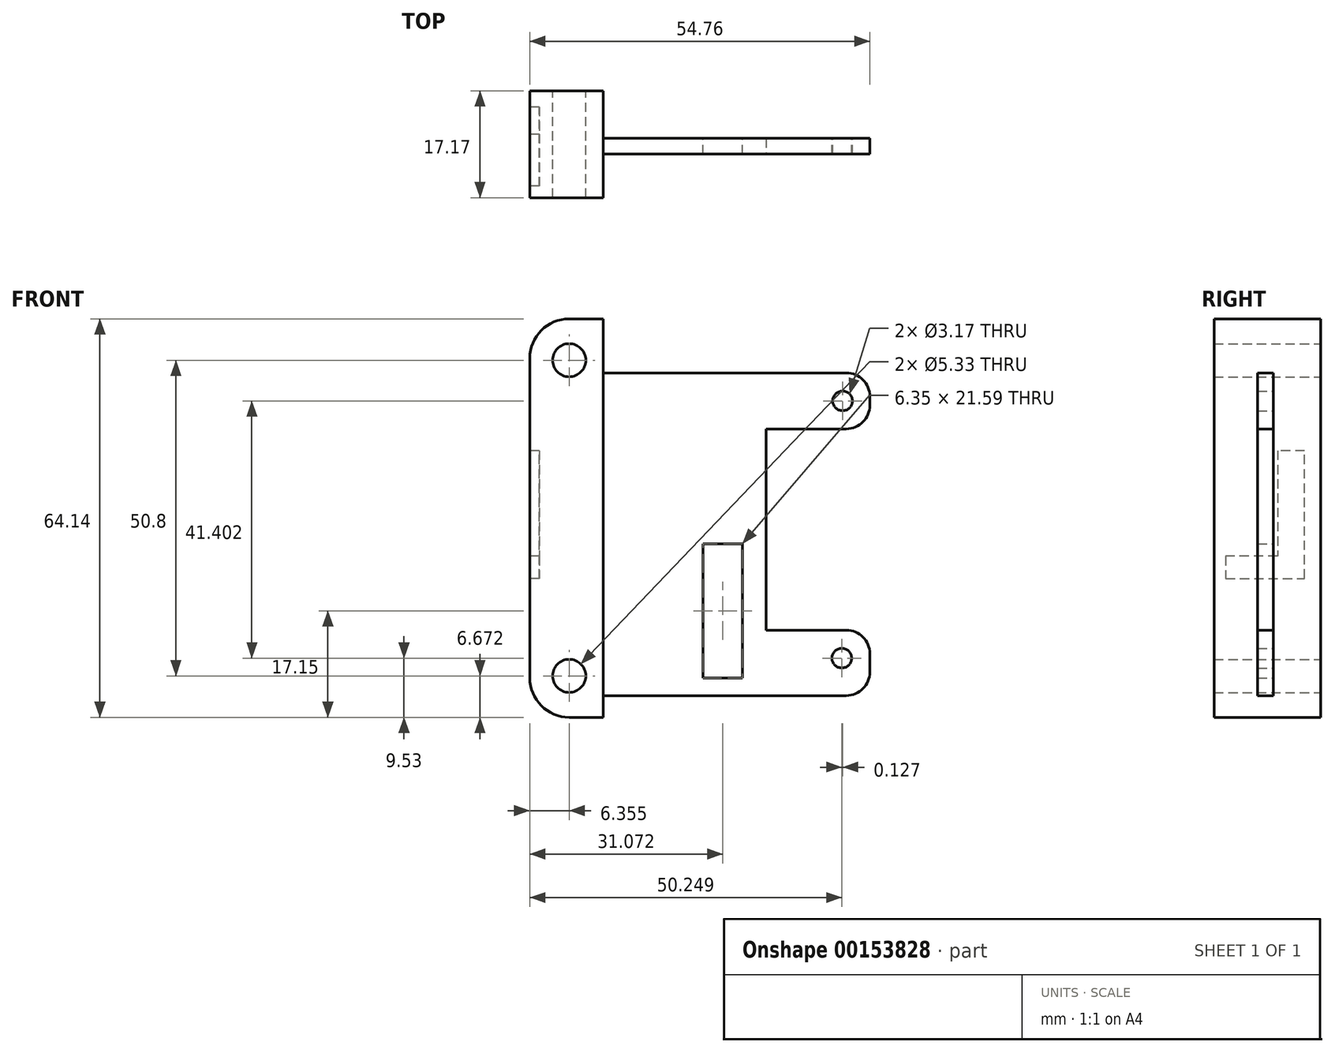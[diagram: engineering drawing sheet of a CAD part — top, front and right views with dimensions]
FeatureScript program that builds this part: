
annotation { "Feature Type Name" : "Feature", "Feature Type Description" : "" }
export const myFeature = defineFeature(function(context is Context, id is Id, definition is map)
    precondition{}
    {
        {
            var Q0;
            Q0=qCreatedBy(makeId("Front.planeOp"),FACE);
            var sketch = newSketch(context, id + "F0", { "sketchPlane" : qUnion([Q0])});
            skCircle(sketch, "E0", {"center": v(-136.53, -6.67) * mm, "radius": 2.67 * mm});
            skCircle(sketch, "E1", {"center": v(-136.53, -57.47) * mm, "radius": 2.67 * mm});
            skLineSegment(sketch, "E2.bottom", {"start": v(-136.53, 0) * mm, "end": v(-85.72, 0) * mm});
            skLineSegment(sketch, "E2.top", {"start": v(-136.53, -64.13) * mm, "end": v(-85.72, -64.13) * mm});
            skLineSegment(sketch, "E2.left", {"start": v(-142.88, -6.35) * mm, "end": v(-142.88, -57.78) * mm});
            skLineSegment(sketch, "E2.right", {"start": v(-85.72, 0) * mm, "end": v(-85.72, -64.13) * mm});
            skPoint(sketch, "E3.visualSharp", {"position": v(-142.88, 0) * mm});
            skArc(sketch, "E3.filletArc", {"start": v(-136.53, 0) * mm, "mid": v(-141.02, -1.86) * mm, "end": v(-142.87, -6.35) * mm});
            skPoint(sketch, "E4.visualSharp", {"position": v(-142.88, -64.13) * mm});
            skArc(sketch, "E4.filletArc", {"start": v(-142.87, -57.78) * mm, "mid": v(-141.02, -62.28) * mm, "end": v(-136.53, -64.13) * mm});
            skCircle(sketch, "E5", {"center": v(-92.5, -13.2) * mm, "radius": 1.59 * mm});
            skLineSegment(sketch, "E6", {"start": v(-136.53, -6.67) * mm, "end": v(-136.53, 0) * mm, "construction": true});
            skLineSegment(sketch, "E7", {"start": v(-136.53, -57.47) * mm, "end": v(-136.53, -64.13) * mm, "construction": true});
            skCircle(sketch, "E8", {"center": v(-92.63, -54.6) * mm, "radius": 1.59 * mm});
            skLineSegment(sketch, "E9.bottom", {"start": v(-114.98, -36.2) * mm, "end": v(-108.63, -36.2) * mm});
            skLineSegment(sketch, "E9.top", {"start": v(-114.98, -57.78) * mm, "end": v(-108.63, -57.78) * mm});
            skLineSegment(sketch, "E9.left", {"start": v(-108.63, -36.2) * mm, "end": v(-108.63, -57.78) * mm});
            skLineSegment(sketch, "E9.right", {"start": v(-114.98, -36.2) * mm, "end": v(-114.98, -57.78) * mm});
            skSolve(sketch);
        }
        {
            var Q0;
            Q0=makeQuery(id+"F0.imprint","IMPRINT",FACE,{"disambiguationData":[TD([[makeQuery(id+"F0.imprint","IMPRINT",EDGE,{"derivedFrom":sQuery(id+"F0.wireOp",EDGE,"E0")}),-1.0]])]});
            var Q1;
            Q1=makeQuery(id+"F0.imprint","IMPRINT",FACE,{"disambiguationData":[TD([[makeQuery(id+"F0.imprint","IMPRINT",EDGE,{"derivedFrom":sQuery(id+"F0.wireOp",EDGE,"01fd989c-5bba-4e2a-9568-51aa30f200c71.MirrorCS")}),1.0]])]});
            extrude(context, id + "F1", {"entities" : qUnion([Q0, Q1]), "depth" : 1.27 * mm});
        }
        {
            var Q0;
            Q0=makeQuery(id+"F1.opExtrude","CAP_FACE",FACE,{"disambiguationData":[OSD([sQuery(id+"F0.wireOp",EDGE,"E0"),sQuery(id+"F0.wireOp",EDGE,"E1"),sQuery(id+"F0.wireOp",EDGE,"E2.bottom"),sQuery(id+"F0.wireOp",EDGE,"E2.top"),sQuery(id+"F0.wireOp",EDGE,"E2.left"),sQuery(id+"F0.wireOp",EDGE,"E2.right"),sQuery(id+"F0.wireOp",EDGE,"E3.filletArc"),sQuery(id+"F0.wireOp",EDGE,"E4.filletArc"),sQuery(id+"F0.wireOp",EDGE,"E5"),sQuery(id+"F0.wireOp",EDGE,"E8"),sQuery(id+"F0.wireOp",EDGE,"E9.bottom"),sQuery(id+"F0.wireOp",EDGE,"E9.top"),sQuery(id+"F0.wireOp",EDGE,"E9.left"),sQuery(id+"F0.wireOp",EDGE,"E9.right")])],"isStart":true});
            var sketch = newSketch(context, id + "F2", { "sketchPlane" : qUnion([Q0])});
            skLineSegment(sketch, "E10", {"start": v(131.05, -64.13) * mm, "end": v(131.05, 0) * mm});
            skLineSegment(sketch, "E11", {"start": v(131.05, 0) * mm, "end": v(136.53, 0) * mm});
            skLineSegment(sketch, "E12", {"start": v(131.05, -64.13) * mm, "end": v(136.53, -64.13) * mm});
            skArc(sketch, "E13", {"start": v(136.53, -64.13) * mm, "mid": v(141.02, -62.28) * mm, "end": v(142.87, -57.78) * mm});
            skArc(sketch, "E14", {"start": v(136.53, 0) * mm, "mid": v(141.02, -1.86) * mm, "end": v(142.87, -6.35) * mm});
            skLineSegment(sketch, "E15", {"start": v(142.88, -57.78) * mm, "end": v(142.87, -6.35) * mm});
            skCircle(sketch, "E16", {"center": v(136.53, -57.47) * mm, "radius": 2.67 * mm});
            skCircle(sketch, "E17", {"center": v(136.53, -6.67) * mm, "radius": 2.67 * mm});
            skSolve(sketch);
        }
        {
            var Q0;
            Q0=makeQuery(id+"F2.imprint","IMPRINT",FACE,{"disambiguationData":[TD([[makeQuery(id+"F2.imprint","IMPRINT",EDGE,{"derivedFrom":sQuery(id+"F2.wireOp",EDGE,"E10")}),-1.0]])]});
            extrude(context, id + "F3", {"entities" : qUnion([Q0]), "operationType" : NewBodyOperationType.ADD, "depth" : 7.62 * mm, "hasSecondDirection" : true, "secondDirectionOppositeDirection" : true, "secondDirectionDepth" : 9.55 * mm});
        }
        {
            var Q0;
            Q0=makeQuery(id+"F3.boolean.opBoolean","MERGE",FACE,{"derivedFrom":[makeQuery(id+"F1.opExtrude","SWEPT_FACE",FACE,{"disambiguationData":[OSD([sQuery(id+"F0.wireOp",EDGE,"E2.left")])]}),makeQuery(id+"F3.opExtrude","SWEPT_FACE",FACE,{"disambiguationData":[OSD([sQuery(id+"F2.wireOp",EDGE,"E15")])]})]});
            var sketch = newSketch(context, id + "F4", { "sketchPlane" : qUnion([Q0])});
            skText(sketch, "E18", { "text": "L", "fontName": "OpenSans-Bold.ttf"});
            const initialGuessF4  = {"E18": [-0.00762, -0.0418, 1, 0, 0.02076]};
            skSetInitialGuess(sketch, initialGuessF4);
            skSolve(sketch);
        }
        {
            var Q0;
            Q0 = qSketchRegion(id + "F4", true);
            extrude(context, id + "F5", {"entities" : qUnion([Q0]), "operationType" : NewBodyOperationType.REMOVE, "oppositeDirection" : true, "depth" : 1.52 * mm});
        }
        {
            var Q0;
            Q0=makeQuery(id+"F1.opExtrude","CAP_FACE",FACE,{"disambiguationData":[OSD([sQuery(id+"F0.wireOp",EDGE,"E0"),sQuery(id+"F0.wireOp",EDGE,"E1"),sQuery(id+"F0.wireOp",EDGE,"E2.bottom"),sQuery(id+"F0.wireOp",EDGE,"E2.top"),sQuery(id+"F0.wireOp",EDGE,"E2.left"),sQuery(id+"F0.wireOp",EDGE,"E2.right"),sQuery(id+"F0.wireOp",EDGE,"E3.filletArc"),sQuery(id+"F0.wireOp",EDGE,"E4.filletArc"),sQuery(id+"F0.wireOp",EDGE,"E5"),sQuery(id+"F0.wireOp",EDGE,"E8"),sQuery(id+"F0.wireOp",EDGE,"E9.bottom"),sQuery(id+"F0.wireOp",EDGE,"E9.top"),sQuery(id+"F0.wireOp",EDGE,"E9.left"),sQuery(id+"F0.wireOp",EDGE,"E9.right")])],"isStart":false});
            var sketch = newSketch(context, id + "F6", { "sketchPlane" : qUnion([Q0])});
            skLineSegment(sketch, "E19", {"start": v(-131.05, 0) * mm, "end": v(-131.05, -8.7) * mm});
            skLineSegment(sketch, "E20", {"start": v(-131.05, -8.7) * mm, "end": v(-88.12, -8.7) * mm});
            skLineSegment(sketch, "E21", {"start": v(-88.12, -8.7) * mm, "end": v(-88.12, -17.72) * mm});
            skLineSegment(sketch, "E22", {"start": v(-88.12, -17.72) * mm, "end": v(-104.82, -17.72) * mm});
            skLineSegment(sketch, "E23", {"start": v(-104.82, -17.72) * mm, "end": v(-104.82, -50.1) * mm});
            skLineSegment(sketch, "E24", {"start": v(-104.82, -50.1) * mm, "end": v(-88.12, -50.1) * mm});
            skLineSegment(sketch, "E25", {"start": v(-88.12, -50.1) * mm, "end": v(-88.12, -60.64) * mm});
            skLineSegment(sketch, "E26", {"start": v(-88.12, -60.64) * mm, "end": v(-131.05, -60.64) * mm});
            skLineSegment(sketch, "E27", {"start": v(-131.05, -60.64) * mm, "end": v(-131.05, -64.13) * mm});
            skLineSegment(sketch, "E28", {"start": v(-131.05, -64.13) * mm, "end": v(-85.72, -64.13) * mm});
            skLineSegment(sketch, "E29", {"start": v(-85.72, -64.13) * mm, "end": v(-85.72, 0) * mm});
            skLineSegment(sketch, "E30", {"start": v(-85.72, 0) * mm, "end": v(-131.05, 0) * mm});
            skSolve(sketch);
        }
        {
            var Q0;
            Q0=makeQuery(id+"F6.imprint","IMPRINT",FACE,{"disambiguationData":[TD([[makeQuery(id+"F6.imprint","IMPRINT",EDGE,{"derivedFrom":sQuery(id+"F6.wireOp",EDGE,"E19")}),-1.0]])]});
            extrude(context, id + "F7", {"entities" : qUnion([Q0]), "operationType" : NewBodyOperationType.REMOVE, "oppositeDirection" : true, "depth" : 25.4 * mm});
        }
        {
            var Q0;
            Q0=makeQuery(id+"F7.boolean.opBoolean","COPY",EDGE,{"derivedFrom":makeQuery(id+"F7.opExtrude","SWEPT_EDGE",EDGE,{"disambiguationData":[OSD([sQuery(id+"F6.wireOp",EDGE,"E20"),sQuery(id+"F6.wireOp",EDGE,"E21")])]})});
            var Q1;
            Q1=makeQuery(id+"F7.boolean.opBoolean","COPY",EDGE,{"derivedFrom":makeQuery(id+"F7.opExtrude","SWEPT_EDGE",EDGE,{"disambiguationData":[OSD([sQuery(id+"F6.wireOp",EDGE,"E24"),sQuery(id+"F6.wireOp",EDGE,"E25")])]})});
            var Q2;
            Q2=makeQuery(id+"F7.boolean.opBoolean","COPY",EDGE,{"derivedFrom":makeQuery(id+"F7.opExtrude","SWEPT_EDGE",EDGE,{"disambiguationData":[OSD([sQuery(id+"F6.wireOp",EDGE,"E25"),sQuery(id+"F6.wireOp",EDGE,"E26")])]})});
            var Q3;
            Q3=makeQuery(id+"F7.boolean.opBoolean","COPY",EDGE,{"derivedFrom":makeQuery(id+"F7.opExtrude","SWEPT_EDGE",EDGE,{"disambiguationData":[OSD([sQuery(id+"F6.wireOp",EDGE,"E21"),sQuery(id+"F6.wireOp",EDGE,"E22")])]})});
            fillet(context, id + "F8", {"entities" : qUnion([Q0, Q1, Q2, Q3]), "radius" : 3.8 * mm, "tangentPropagation" : true, "allowEdgeOverflow" : false});
        }
        {
            var Q0;
            Q0=makeQuery(id+"F1.opExtrude","CAP_FACE",FACE,{"disambiguationData":[OSD([sQuery(id+"F0.wireOp",EDGE,"E0"),sQuery(id+"F0.wireOp",EDGE,"E1"),sQuery(id+"F0.wireOp",EDGE,"E2.bottom"),sQuery(id+"F0.wireOp",EDGE,"E2.top"),sQuery(id+"F0.wireOp",EDGE,"E2.left"),sQuery(id+"F0.wireOp",EDGE,"E2.right"),sQuery(id+"F0.wireOp",EDGE,"E3.filletArc"),sQuery(id+"F0.wireOp",EDGE,"E4.filletArc"),sQuery(id+"F0.wireOp",EDGE,"E5"),sQuery(id+"F0.wireOp",EDGE,"E8"),sQuery(id+"F0.wireOp",EDGE,"E9.bottom"),sQuery(id+"F0.wireOp",EDGE,"E9.top"),sQuery(id+"F0.wireOp",EDGE,"E9.left"),sQuery(id+"F0.wireOp",EDGE,"E9.right")])],"isStart":false});
            var sketch = newSketch(context, id + "F9", { "sketchPlane" : qUnion([Q0])});
            skLineSegment(sketch, "E31.bottom", {"start": v(-131.05, -8.7) * mm, "end": v(-91.93, -8.7) * mm});
            skLineSegment(sketch, "E31.top", {"start": v(-131.05, -60.64) * mm, "end": v(-91.93, -60.64) * mm});
            skLineSegment(sketch, "E31.left", {"start": v(-131.05, -8.7) * mm, "end": v(-131.05, -60.64) * mm});
            skLineSegment(sketch, "E32.bottom", {"start": v(-104.82, -50.1) * mm, "end": v(-91.93, -50.1) * mm});
            skLineSegment(sketch, "E32.top", {"start": v(-104.82, -17.72) * mm, "end": v(-91.93, -17.72) * mm});
            skLineSegment(sketch, "E32.left", {"start": v(-104.82, -50.1) * mm, "end": v(-104.82, -17.72) * mm});
            skLineSegment(sketch, "E33.bottom", {"start": v(-114.98, -36.2) * mm, "end": v(-108.63, -36.2) * mm});
            skLineSegment(sketch, "E33.top", {"start": v(-114.98, -57.78) * mm, "end": v(-108.63, -57.78) * mm});
            skLineSegment(sketch, "E33.left", {"start": v(-114.98, -36.2) * mm, "end": v(-114.98, -57.78) * mm});
            skLineSegment(sketch, "E33.right", {"start": v(-108.63, -36.2) * mm, "end": v(-108.63, -57.78) * mm});
            skLineSegment(sketch, "E34", {"start": v(-88.12, -12.5) * mm, "end": v(-88.12, -13.9) * mm});
            skLineSegment(sketch, "E35", {"start": v(-88.12, -53.91) * mm, "end": v(-88.12, -56.83) * mm});
            skArc(sketch, "E36", {"start": v(-91.93, -8.7) * mm, "mid": v(-89.24, -9.82) * mm, "end": v(-88.12, -12.5) * mm});
            skArc(sketch, "E37", {"start": v(-88.12, -13.9) * mm, "mid": v(-89.24, -16.6) * mm, "end": v(-91.93, -17.72) * mm});
            skArc(sketch, "E38", {"start": v(-91.93, -50.1) * mm, "mid": v(-89.24, -51.22) * mm, "end": v(-88.12, -53.91) * mm});
            skArc(sketch, "E39", {"start": v(-88.12, -56.83) * mm, "mid": v(-89.24, -59.53) * mm, "end": v(-91.93, -60.64) * mm});
            skCircle(sketch, "E40", {"center": v(-92.63, -54.6) * mm, "radius": 1.59 * mm});
            skCircle(sketch, "E41", {"center": v(-92.5, -13.2) * mm, "radius": 1.59 * mm});
            skSolve(sketch);
        }
        {
            var Q0;
            Q0 = qSketchRegion(id + "F9", true);
            extrude(context, id + "F10", {"entities" : qUnion([Q0]), "operationType" : NewBodyOperationType.ADD, "depth" : 1.27 * mm});
        }
    });
